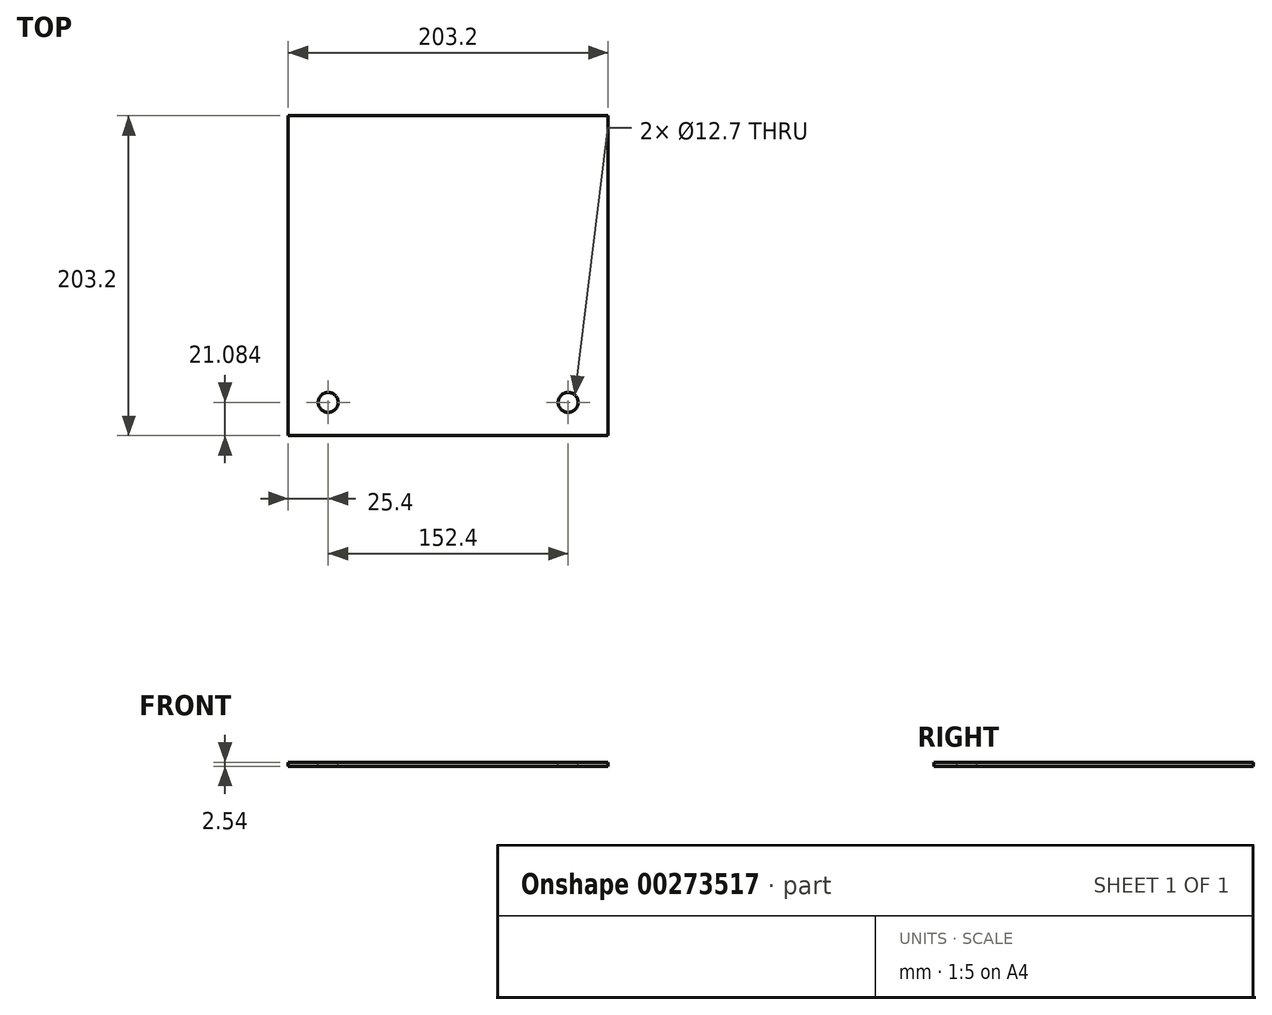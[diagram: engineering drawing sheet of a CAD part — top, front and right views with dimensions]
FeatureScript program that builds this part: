
annotation { "Feature Type Name" : "Feature", "Feature Type Description" : "" }
export const myFeature = defineFeature(function(context is Context, id is Id, definition is map)
    precondition{}
    {
        {
            var Q0;
            Q0=qCreatedBy(makeId("Top.planeOp"),FACE);
            var sketch = newSketch(context, id + "F0", { "sketchPlane" : qUnion([Q0])});
            skLineSegment(sketch, "E0.bottom", {"start": v(0, 0) * mm, "end": v(-203.2, 0) * mm});
            skLineSegment(sketch, "E0.top", {"start": v(0, 203.2) * mm, "end": v(-203.2, 203.2) * mm});
            skLineSegment(sketch, "E0.left", {"start": v(0, 0) * mm, "end": v(0, 203.2) * mm});
            skLineSegment(sketch, "E0.right", {"start": v(-203.2, 0) * mm, "end": v(-203.2, 203.2) * mm});
            skSolve(sketch);
        }
        {
            var Q0;
            Q0=makeQuery(id+"F0.imprint","IMPRINT",FACE,{"disambiguationData":[TD([[makeQuery(id+"F0.imprint","IMPRINT",EDGE,{"derivedFrom":sQuery(id+"F0.wireOp",EDGE,"E0.bottom")}),-1.0]])]});
            extrude(context, id + "F1", {"entities" : qUnion([Q0]), "depth" : 2.54 * mm});
        }
        {
            var Q0;
            Q0=makeQuery(id+"F1.opExtrude","CAP_FACE",FACE,{"disambiguationData":[OSD([sQuery(id+"F0.wireOp",EDGE,"E0.bottom"),sQuery(id+"F0.wireOp",EDGE,"E0.top"),sQuery(id+"F0.wireOp",EDGE,"E0.left"),sQuery(id+"F0.wireOp",EDGE,"E0.right")])],"isStart":false});
            var sketch = newSketch(context, id + "F2", { "sketchPlane" : qUnion([Q0])});
            skCircle(sketch, "E1", {"center": v(-177.8, 21.08) * mm, "radius": 6.35 * mm});
            skCircle(sketch, "E2", {"center": v(-25.4, 21.08) * mm, "radius": 6.35 * mm});
            skLineSegment(sketch, "E3", {"start": v(-177.8, 21.08) * mm, "end": v(-203.2, 21.08) * mm});
            skLineSegment(sketch, "E4", {"start": v(-25.4, 21.08) * mm, "end": v(0, 21.08) * mm});
            skSolve(sketch);
        }
        {
            var Q0;
            Q0=makeQuery(id+"F2.imprint","IMPRINT",FACE,{"disambiguationData":[TD([[makeQuery(id+"F2.imprint","IMPRINT",EDGE,{"derivedFrom":sQuery(id+"F2.wireOp",EDGE,"E1")}),1.0]])]});
            extrude(context, id + "F3", {"entities" : qUnion([Q0]), "operationType" : NewBodyOperationType.REMOVE, "oppositeDirection" : true, "depth" : 25.4 * mm});
        }
        {
            var Q0;
            Q0 = qSketchRegion(id + "F2", true);
            extrude(context, id + "F4", {"entities" : qUnion([Q0]), "operationType" : NewBodyOperationType.REMOVE, "oppositeDirection" : true, "depth" : 25.4 * mm});
        }
    });
